# Revit family: Plymold-Essentials-Legacy_Seating
name_source: partatom
category: Furniture
units: mm (PartAtom-declared; Revit-internal decimal feet)

## family parameters
Always vertical = Yes
Cut with Voids When Loaded = No
OmniClass Number = 23.40.20.00
OmniClass Title = General Furniture and Specialties
Render Appearance Source = Family Geometry
Room Calculation Point = No
Shared = No
Work Plane-Based = No

## types (2) — shared parameters
Assembly Code = E2020200
Brand = Legacy
Default Elevation = 0"
Depth = 20 1/2"
FRAME MATERIAL = PLY - Iron Glimme Powdercoat
GLIDES MATERIAL = PLY - Plastic Black
Keynote = 12500
Manufacturer = Plymold
Product Documentation Link = https://plymold.com
Revit Model Built By = https://www.servex-us.com
SHELL MATERIAL = PLY - Wood Mahogany - Vertical
Sustainability = https://plymold.com
Type Comments = Chairs & Barstools
URL = https://plymold.com
Width = 17"
zero-valued in all types: Cost

## per-type parameters (varying)
| type | Description | Height |
| 6771 | Legacy Chair - 17”W x 20 1/2”D x 33”H | 33" |
| 6773 | Legacy Barstool - 17”W x 20 1/2”D x 45 1/2”H | 45 1/2" |

note: column(s) folded — value = type name in every type: Model

## geometry (parser evidence)
native form markers: Sweep x8
no freeform markers — native parametric forms only
